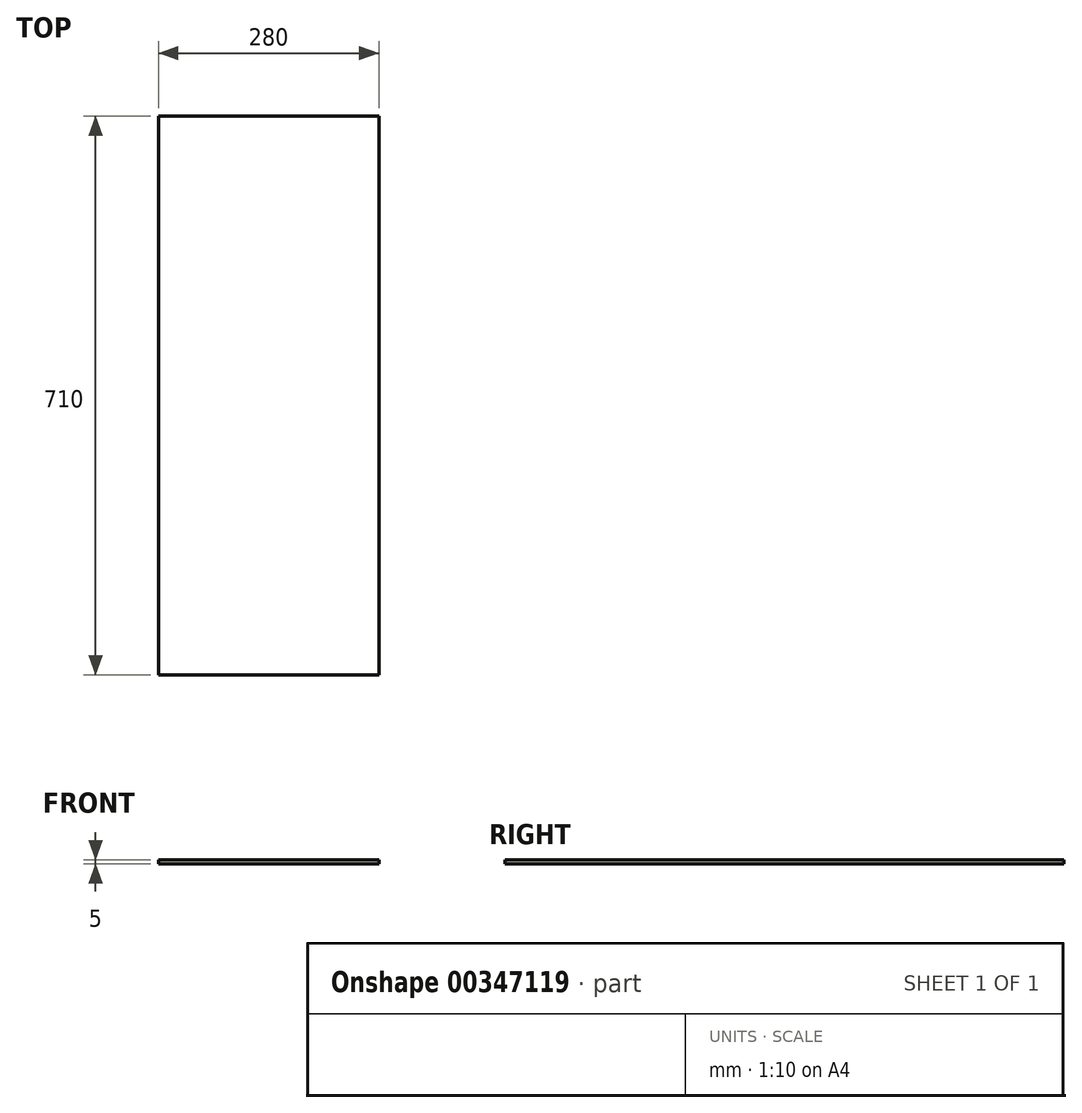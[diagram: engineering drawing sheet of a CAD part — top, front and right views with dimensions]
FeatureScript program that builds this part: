
annotation { "Feature Type Name" : "Feature", "Feature Type Description" : "" }
export const myFeature = defineFeature(function(context is Context, id is Id, definition is map)
    precondition{}
    {
        {
            var Q0;
            Q0=qCreatedBy(makeId("Top.planeOp"),FACE);
            var sketch = newSketch(context, id + "F0", { "sketchPlane" : qUnion([Q0])});
            skLineSegment(sketch, "E0.bottom", {"start": v(-140, 355) * mm, "end": v(140, 355) * mm});
            skLineSegment(sketch, "E0.top", {"start": v(-140, -355) * mm, "end": v(140, -355) * mm});
            skLineSegment(sketch, "E0.left", {"start": v(-140, 355) * mm, "end": v(-140, -355) * mm});
            skLineSegment(sketch, "E0.right", {"start": v(140, 355) * mm, "end": v(140, -355) * mm});
            skPoint(sketch, "E0.middle", {"position": v(0, 0) * mm});
            skSolve(sketch);
        }
        {
            var Q0;
            Q0 = qSketchRegion(id + "F0", true);
            extrude(context, id + "F1", {"entities" : qUnion([Q0]), "depth" : 5 * mm});
        }
    });
